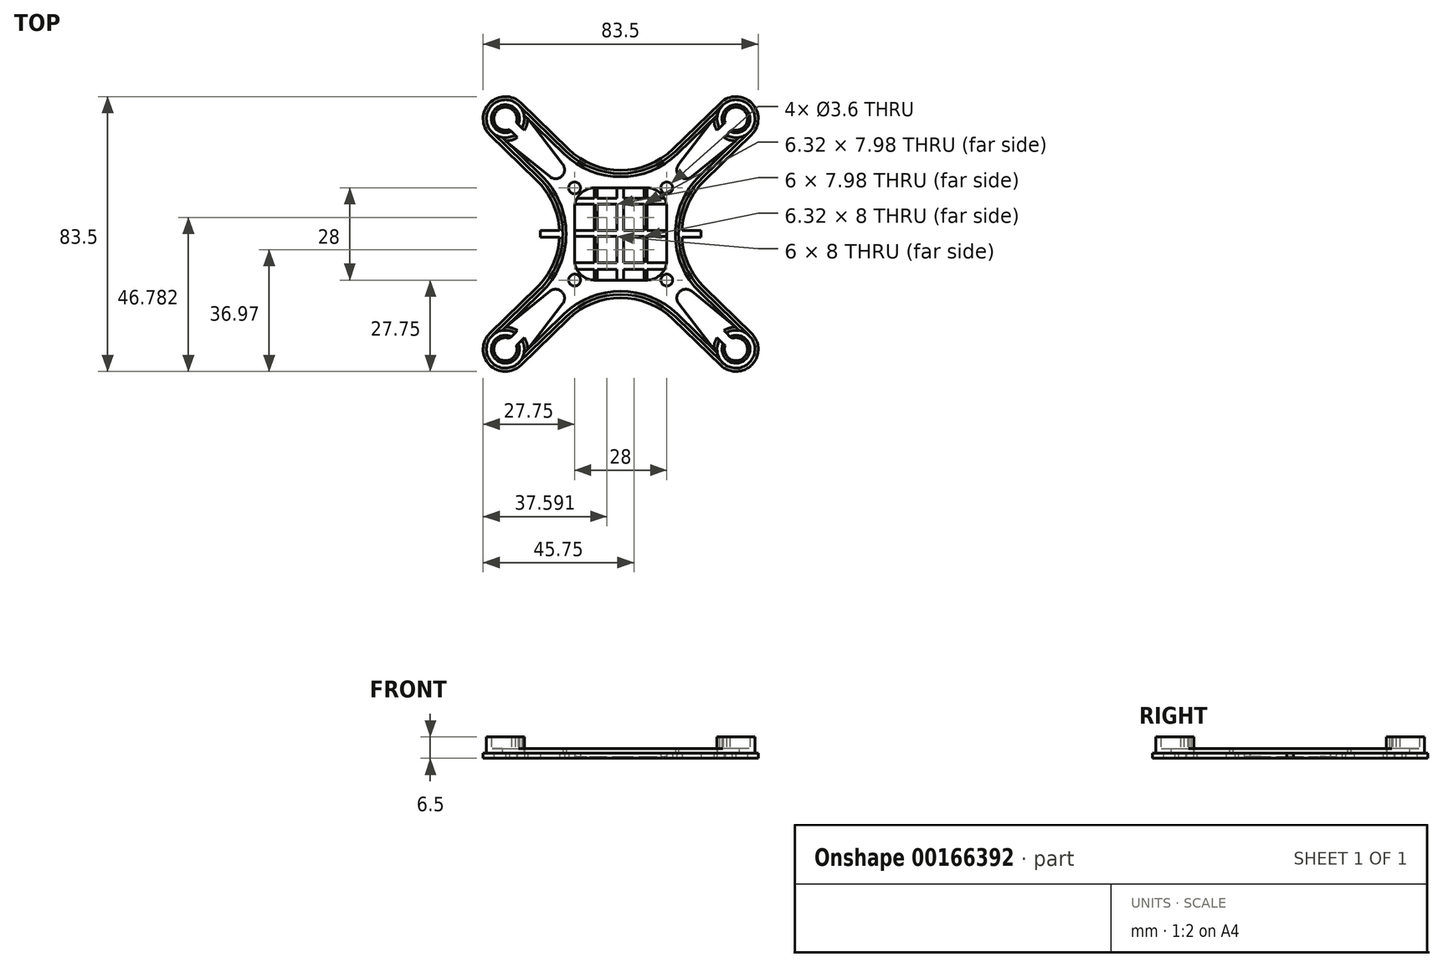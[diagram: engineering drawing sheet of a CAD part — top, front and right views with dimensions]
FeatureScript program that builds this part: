
annotation { "Feature Type Name" : "Feature", "Feature Type Description" : "" }
export const myFeature = defineFeature(function(context is Context, id is Id, definition is map)
    precondition{}
    {
        {
            var Q0;
            Q0=qCreatedBy(makeId("Top.planeOp"),FACE);
            var sketch = newSketch(context, id + "F0", { "sketchPlane" : qUnion([Q0])});
            skArc(sketch, "E0", {"start": v(31.69, -33.87) * mm, "mid": v(37.5, -37.44) * mm, "end": v(33.78, -31.72) * mm});
            skArc(sketch, "E1", {"start": v(29.24, -31.49) * mm, "mid": v(28.5, -33.2) * mm, "end": v(28.25, -35.06) * mm});
            skCircle(sketch, "E2", {"center": v(14, -14) * mm, "radius": 1.8 * mm});
            skLineSegment(sketch, "E3.0", {"start": v(39.7, -30.16) * mm, "end": v(25.47, -16.32) * mm});
            skLineSegment(sketch, "E4.0", {"start": v(30.3, -39.84) * mm, "end": v(15.88, -25.83) * mm});
            skArc(sketch, "E5", {"start": v(25.47, 16.32) * mm, "mid": v(18.58, 0) * mm, "end": v(25.47, -16.32) * mm});
            skArc(sketch, "E6.MirrorCS", {"start": v(-15.88, -25.83) * mm, "mid": v(0, -19.38) * mm, "end": v(15.88, -25.83) * mm});
            skPoint(sketch, "E7.orphan", {"position": v(7.32, -17.5) * mm});
            skArc(sketch, "E8", {"start": v(21.52, -17.39) * mm, "mid": v(17.87, -17.55) * mm, "end": v(17.6, -21.2) * mm});
            skLineSegment(sketch, "E9", {"start": v(31.69, -33.87) * mm, "end": v(29.24, -31.49) * mm});
            skLineSegment(sketch, "E10", {"start": v(31.33, -29.34) * mm, "end": v(33.78, -31.72) * mm});
            skArc(sketch, "E11.trimOffspring", {"start": v(34.87, -28.25) * mm, "mid": v(33.02, -28.55) * mm, "end": v(31.33, -29.34) * mm});
            skArc(sketch, "E12.trimOffspring", {"start": v(30.3, -39.84) * mm, "mid": v(39.84, -39.7) * mm, "end": v(39.7, -30.16) * mm});
            skLineSegment(sketch, "E13", {"start": v(8, -14) * mm, "end": v(-9, -14) * mm});
            skLineSegment(sketch, "E14", {"start": v(14, -8) * mm, "end": v(14, 9) * mm});
            skArc(sketch, "E15.filletArc", {"start": v(8, -14) * mm, "mid": v(12.24, -12.24) * mm, "end": v(14, -8) * mm});
            skLineSegment(sketch, "E16", {"start": v(28.25, -35.06) * mm, "end": v(17.6, -21.2) * mm});
            skLineSegment(sketch, "E17", {"start": v(34.87, -28.25) * mm, "end": v(21.52, -17.39) * mm});
            skLineSegment(sketch, "E18.MirrorCS", {"start": v(-31.33, -29.34) * mm, "end": v(-33.78, -31.72) * mm});
            skArc(sketch, "E19.MirrorCS", {"start": v(-29.24, -31.49) * mm, "mid": v(-28.5, -33.2) * mm, "end": v(-28.25, -35.06) * mm});
            skLineSegment(sketch, "E20.MirrorCS", {"start": v(-31.69, -33.87) * mm, "end": v(-29.24, -31.49) * mm});
            skArc(sketch, "E21.MirrorCS", {"start": v(-34.87, -28.25) * mm, "mid": v(-33.02, -28.55) * mm, "end": v(-31.33, -29.34) * mm});
            skLineSegment(sketch, "E22.MirrorCS", {"start": v(-34.87, -28.25) * mm, "end": v(-21.52, -17.39) * mm});
            skLineSegment(sketch, "E23.MirrorCS", {"start": v(-30.3, -39.84) * mm, "end": v(-15.88, -25.83) * mm});
            skArc(sketch, "E24.MirrorCS", {"start": v(-21.52, -17.39) * mm, "mid": v(-17.87, -17.55) * mm, "end": v(-17.6, -21.2) * mm});
            skLineSegment(sketch, "E25.MirrorCS", {"start": v(-39.7, -30.16) * mm, "end": v(-25.47, -16.32) * mm});
            skArc(sketch, "E26.MirrorCS", {"start": v(-31.69, -33.87) * mm, "mid": v(-37.5, -37.44) * mm, "end": v(-33.78, -31.72) * mm});
            skArc(sketch, "E27.MirrorCS", {"start": v(-30.3, -39.84) * mm, "mid": v(-39.84, -39.7) * mm, "end": v(-39.7, -30.16) * mm});
            skLineSegment(sketch, "E28.MirrorCS", {"start": v(-28.25, -35.06) * mm, "end": v(-17.6, -21.2) * mm});
            skCircle(sketch, "E29.MirrorC", {"center": v(-14, -14) * mm, "radius": 1.8 * mm});
            skArc(sketch, "E30.MirrorCS", {"start": v(-8, -14) * mm, "mid": v(-12.24, -12.24) * mm, "end": v(-14, -8) * mm});
            skArc(sketch, "E31.MirrorCS", {"start": v(-25.47, 16.32) * mm, "mid": v(-18.58, 0) * mm, "end": v(-25.47, -16.32) * mm});
            skLineSegment(sketch, "E32.MirrorCS", {"start": v(-14, -8) * mm, "end": v(-14, 9) * mm});
            skLineSegment(sketch, "E33.MirrorCS", {"start": v(-8, -14) * mm, "end": v(9, -14) * mm});
            skPoint(sketch, "E34.MirrorP", {"position": v(-7.32, -17.5) * mm});
            skLineSegment(sketch, "E35.MirrorCS", {"start": v(-31.69, 33.87) * mm, "end": v(-29.24, 31.49) * mm});
            skCircle(sketch, "E36.MirrorC", {"center": v(-14, 14) * mm, "radius": 1.8 * mm});
            skArc(sketch, "E37.MirrorCS", {"start": v(34.87, 28.25) * mm, "mid": v(33.02, 28.55) * mm, "end": v(31.33, 29.34) * mm});
            skLineSegment(sketch, "E38.MirrorCS", {"start": v(-31.33, 29.34) * mm, "end": v(-33.78, 31.72) * mm});
            skCircle(sketch, "E39.MirrorC", {"center": v(14, 14) * mm, "radius": 1.8 * mm});
            skLineSegment(sketch, "E40.MirrorCS", {"start": v(31.69, 33.87) * mm, "end": v(29.24, 31.49) * mm});
            skArc(sketch, "E41.MirrorCS", {"start": v(-34.87, 28.25) * mm, "mid": v(-33.02, 28.55) * mm, "end": v(-31.33, 29.34) * mm});
            skLineSegment(sketch, "E42.MirrorCS", {"start": v(31.33, 29.34) * mm, "end": v(33.78, 31.72) * mm});
            skArc(sketch, "E43.MirrorCS", {"start": v(29.24, 31.49) * mm, "mid": v(28.5, 33.2) * mm, "end": v(28.25, 35.06) * mm});
            skArc(sketch, "E44.MirrorCS", {"start": v(-29.24, 31.49) * mm, "mid": v(-28.5, 33.2) * mm, "end": v(-28.25, 35.06) * mm});
            skArc(sketch, "E45.MirrorCS", {"start": v(8, 14) * mm, "mid": v(12.24, 12.24) * mm, "end": v(14, 8) * mm});
            skArc(sketch, "E46.MirrorCS", {"start": v(-8, 14) * mm, "mid": v(-12.24, 12.24) * mm, "end": v(-14, 8) * mm});
            skLineSegment(sketch, "E47.MirrorCS", {"start": v(8, 14) * mm, "end": v(-9, 14) * mm});
            skPoint(sketch, "E48.MirrorP", {"position": v(7.32, 17.5) * mm});
            skArc(sketch, "E49.MirrorCS", {"start": v(21.52, 17.39) * mm, "mid": v(17.87, 17.55) * mm, "end": v(17.6, 21.2) * mm});
            skArc(sketch, "E50.MirrorCS", {"start": v(-30.3, 39.84) * mm, "mid": v(-39.84, 39.7) * mm, "end": v(-39.7, 30.16) * mm});
            skLineSegment(sketch, "E51.MirrorCS", {"start": v(34.87, 28.25) * mm, "end": v(21.52, 17.39) * mm});
            skPoint(sketch, "E52.MirrorP", {"position": v(-7.32, 17.5) * mm});
            skArc(sketch, "E53.MirrorCS", {"start": v(-15.88, 25.83) * mm, "mid": v(0, 19.38) * mm, "end": v(15.88, 25.83) * mm});
            skArc(sketch, "E54.MirrorCS", {"start": v(-21.52, 17.39) * mm, "mid": v(-17.87, 17.55) * mm, "end": v(-17.6, 21.2) * mm});
            skLineSegment(sketch, "E55.MirrorCS", {"start": v(-34.87, 28.25) * mm, "end": v(-21.52, 17.39) * mm});
            skLineSegment(sketch, "E56.MirrorCS", {"start": v(30.3, 39.84) * mm, "end": v(15.88, 25.83) * mm});
            skArc(sketch, "E57.MirrorCS", {"start": v(-31.69, 33.87) * mm, "mid": v(-37.5, 37.44) * mm, "end": v(-33.78, 31.72) * mm});
            skLineSegment(sketch, "E58.MirrorCS", {"start": v(-28.25, 35.06) * mm, "end": v(-17.6, 21.2) * mm});
            skLineSegment(sketch, "E59.MirrorCS", {"start": v(39.7, 30.16) * mm, "end": v(25.47, 16.32) * mm});
            skLineSegment(sketch, "E60.MirrorCS", {"start": v(-8, 14) * mm, "end": v(9, 14) * mm});
            skArc(sketch, "E61.MirrorCS", {"start": v(31.69, 33.87) * mm, "mid": v(37.5, 37.44) * mm, "end": v(33.78, 31.72) * mm});
            skLineSegment(sketch, "E62.MirrorCS", {"start": v(-39.7, 30.16) * mm, "end": v(-25.47, 16.32) * mm});
            skLineSegment(sketch, "E63.MirrorCS", {"start": v(-30.3, 39.84) * mm, "end": v(-15.88, 25.83) * mm});
            skLineSegment(sketch, "E64.MirrorCS", {"start": v(-14, 8) * mm, "end": v(-14, -9) * mm});
            skArc(sketch, "E65.MirrorCS", {"start": v(30.3, 39.84) * mm, "mid": v(39.84, 39.7) * mm, "end": v(39.7, 30.16) * mm});
            skLineSegment(sketch, "E66.MirrorCS", {"start": v(14, 8) * mm, "end": v(14, -9) * mm});
            skLineSegment(sketch, "E67.MirrorCS", {"start": v(28.25, 35.06) * mm, "end": v(17.6, 21.2) * mm});
            skLineSegment(sketch, "E68.bottom", {"start": v(18.4, 1) * mm, "end": v(24.4, 1) * mm});
            skLineSegment(sketch, "E68.top", {"start": v(18.4, -1) * mm, "end": v(24.4, -1) * mm});
            skLineSegment(sketch, "E68.left", {"start": v(18.4, 1) * mm, "end": v(18.4, -1) * mm});
            skLineSegment(sketch, "E68.right", {"start": v(24.4, 1) * mm, "end": v(24.4, -1) * mm});
            skLineSegment(sketch, "E69.MirrorCS", {"start": v(-18.4, 1) * mm, "end": v(-18.4, -1) * mm});
            skLineSegment(sketch, "E70.MirrorCS", {"start": v(-18.4, -1) * mm, "end": v(-24.4, -1) * mm});
            skLineSegment(sketch, "E71.MirrorCS", {"start": v(-24.4, 1) * mm, "end": v(-24.4, -1) * mm});
            skLineSegment(sketch, "E72.MirrorCS", {"start": v(-18.4, 1) * mm, "end": v(-24.4, 1) * mm});
            skSolve(sketch);
        }
        {
            var Q0;
            Q0 = qSketchRegion(id + "F0", true);
            extrude(context, id + "F1", {"entities" : qUnion([Q0]), "depth" : 1.5 * mm});
        }
        {
            var Q0;
            Q0=makeQuery(id+"F1.opExtrude","CAP_FACE",FACE,{"disambiguationData":[OSD([sQuery(id+"F0.wireOp",EDGE,"E0"),sQuery(id+"F0.wireOp",EDGE,"E1"),sQuery(id+"F0.wireOp",EDGE,"a01uJ8fQ-2ShT-JJJs-khPB-feFI2KhJfNbK"),sQuery(id+"F0.wireOp",EDGE,"Ob7BAK0L-Im8b-nV2W-ZPOP-jmZc5u1GQHVQ"),sQuery(id+"F0.wireOp",EDGE,"Yhxhbh3N-Pwvf-CZAK-NTRz-WfjfcWOoB3H8"),sQuery(id+"F0.wireOp",EDGE,"E2"),sQuery(id+"F0.wireOp",EDGE,"E3.0"),sQuery(id+"F0.wireOp",EDGE,"E4.0"),sQuery(id+"F0.wireOp",EDGE,"921c4a34-4074-4e6a-8ea0-2c27b11e1a93.0"),sQuery(id+"F0.wireOp",EDGE,"8042876e-c550-468f-ba5b-50dd2e758e40.0"),sQuery(id+"F0.wireOp",EDGE,"E5"),sQuery(id+"F0.wireOp",EDGE,"b88f5849-8e9e-4a16-b14d-f28babdcc0c70.MirrorCS"),sQuery(id+"F0.wireOp",EDGE,"b88f5849-8e9e-4a16-b14d-f28babdcc0c71.MirrorCS"),sQuery(id+"F0.wireOp",EDGE,"b88f5849-8e9e-4a16-b14d-f28babdcc0c74.MirrorCS"),sQuery(id+"F0.wireOp",EDGE,"b88f5849-8e9e-4a16-b14d-f28babdcc0c75.MirrorCS"),sQuery(id+"F0.wireOp",EDGE,"b8554301-71cc-457b-a27f-fdabd42372d80.MirrorCS"),sQuery(id+"F0.wireOp",EDGE,"8d917b84-10ed-46aa-9923-405c7a226399.filletArc"),sQuery(id+"F0.wireOp",EDGE,"E6.MirrorCS"),sQuery(id+"F0.wireOp",EDGE,"a4643b09-8a2d-470e-a5d3-b5b7147de01a.trimOffspring"),sQuery(id+"F0.wireOp",EDGE,"e1d1502e-aa15-4543-9f89-ce20ea1ce206.trimOffspring"),sQuery(id+"F0.wireOp",EDGE,"E8"),sQuery(id+"F0.wireOp",EDGE,"432c7407-925d-4150-9526-7c587b8a6b590.MirrorCS"),sQuery(id+"F0.wireOp",EDGE,"432c7407-925d-4150-9526-7c587b8a6b591.MirrorCS"),sQuery(id+"F0.wireOp",EDGE,"432c7407-925d-4150-9526-7c587b8a6b592.MirrorCS"),sQuery(id+"F0.wireOp",EDGE,"84ef0a4b-eb97-41a7-a49f-92f9b87771770.MirrorCS"),sQuery(id+"F0.wireOp",EDGE,"84ef0a4b-eb97-41a7-a49f-92f9b87771771.MirrorCS"),sQuery(id+"F0.wireOp",EDGE,"84ef0a4b-eb97-41a7-a49f-92f9b87771772.MirrorCS"),sQuery(id+"F0.wireOp",EDGE,"84ef0a4b-eb97-41a7-a49f-92f9b87771773.MirrorCS"),sQuery(id+"F0.wireOp",EDGE,"84ef0a4b-eb97-41a7-a49f-92f9b87771774.MirrorCS"),sQuery(id+"F0.wireOp",EDGE,"84ef0a4b-eb97-41a7-a49f-92f9b87771775.MirrorCS"),sQuery(id+"F0.wireOp",EDGE,"feb3afbb-cc8c-4bbc-aa67-0586ad6dce8c.0"),sQuery(id+"F0.wireOp",EDGE,"a1452b85-d45b-435e-881a-8c6a6ef33bc9.0"),sQuery(id+"F0.wireOp",EDGE,"64c3a18d-b4ba-416d-8e09-7861b4cc0028.0"),sQuery(id+"F0.wireOp",EDGE,"76b5986a-2c51-4484-8229-e95649198d5d.0"),sQuery(id+"F0.wireOp",EDGE,"E9"),sQuery(id+"F0.wireOp",EDGE,"E10"),sQuery(id+"F0.wireOp",EDGE,"E11.trimOffspring"),sQuery(id+"F0.wireOp",EDGE,"E12.trimOffspring"),sQuery(id+"F0.wireOp",EDGE,"e6a221e6-ec1e-47e5-89df-8c310038d3240.MirrorCS"),sQuery(id+"F0.wireOp",EDGE,"e6a221e6-ec1e-47e5-89df-8c310038d3241.MirrorCS"),sQuery(id+"F0.wireOp",EDGE,"e6a221e6-ec1e-47e5-89df-8c310038d3242.MirrorCS"),sQuery(id+"F0.wireOp",EDGE,"e6a221e6-ec1e-47e5-89df-8c310038d3244.MirrorCS"),sQuery(id+"F0.wireOp",EDGE,"e6a221e6-ec1e-47e5-89df-8c310038d3245.MirrorCS"),sQuery(id+"F0.wireOp",EDGE,"e6a221e6-ec1e-47e5-89df-8c310038d3246.MirrorCS"),sQuery(id+"F0.wireOp",EDGE,"1c5d13f6-029d-4adf-95b2-7eb6a2bd37fe0.MirrorCS"),sQuery(id+"F0.wireOp",EDGE,"1c5d13f6-029d-4adf-95b2-7eb6a2bd37fe1.MirrorCS"),sQuery(id+"F0.wireOp",EDGE,"1c5d13f6-029d-4adf-95b2-7eb6a2bd37fe2.MirrorCS"),sQuery(id+"F0.wireOp",EDGE,"1c5d13f6-029d-4adf-95b2-7eb6a2bd37fe3.MirrorCS"),sQuery(id+"F0.wireOp",EDGE,"1c5d13f6-029d-4adf-95b2-7eb6a2bd37fe5.MirrorCS"),sQuery(id+"F0.wireOp",EDGE,"1c5d13f6-029d-4adf-95b2-7eb6a2bd37fe6.MirrorCS"),sQuery(id+"F0.wireOp",EDGE,"1c5d13f6-029d-4adf-95b2-7eb6a2bd37fe7.MirrorCS"),sQuery(id+"F0.wireOp",EDGE,"1c5d13f6-029d-4adf-95b2-7eb6a2bd37fe8.MirrorCS"),sQuery(id+"F0.wireOp",EDGE,"1c5d13f6-029d-4adf-95b2-7eb6a2bd37fe9.MirrorCS"),sQuery(id+"F0.wireOp",EDGE,"1c5d13f6-029d-4adf-95b2-7eb6a2bd37fe10.MirrorCS"),sQuery(id+"F0.wireOp",EDGE,"1c5d13f6-029d-4adf-95b2-7eb6a2bd37fe12.MirrorCS"),sQuery(id+"F0.wireOp",EDGE,"1c5d13f6-029d-4adf-95b2-7eb6a2bd37fe13.MirrorCS")])],"isStart":false});
            var sketch = newSketch(context, id + "F2", { "sketchPlane" : qUnion([Q0])});
            skLineSegment(sketch, "E73.0", {"start": v(32.07, -30.06) * mm, "end": v(33.2, -31.15) * mm});
            skLineSegment(sketch, "E73.1", {"start": v(31.1, -33.3) * mm, "end": v(29.97, -32.2) * mm});
            skArc(sketch, "E74", {"start": v(31.1, -33.3) * mm, "mid": v(38.05, -37.96) * mm, "end": v(33.2, -31.15) * mm});
            skArc(sketch, "E75", {"start": v(29.97, -32.2) * mm, "mid": v(39.12, -39) * mm, "end": v(32.07, -30.06) * mm});
            skLineSegment(sketch, "E76.MirrorCS", {"start": v(-32.07, -30.06) * mm, "end": v(-33.2, -31.15) * mm});
            skLineSegment(sketch, "E77.MirrorCS", {"start": v(-31.1, -33.3) * mm, "end": v(-29.97, -32.2) * mm});
            skArc(sketch, "E78.MirrorCS", {"start": v(-31.1, -33.3) * mm, "mid": v(-38.05, -37.96) * mm, "end": v(-33.2, -31.15) * mm});
            skArc(sketch, "E79.MirrorCS", {"start": v(-29.97, -32.2) * mm, "mid": v(-39.12, -39) * mm, "end": v(-32.07, -30.06) * mm});
            skLineSegment(sketch, "E80.MirrorCS", {"start": v(32.07, 30.06) * mm, "end": v(33.2, 31.15) * mm});
            skLineSegment(sketch, "E81.MirrorCS", {"start": v(31.1, 33.3) * mm, "end": v(29.97, 32.2) * mm});
            skLineSegment(sketch, "E82.MirrorCS", {"start": v(-31.1, 33.3) * mm, "end": v(-29.97, 32.2) * mm});
            skLineSegment(sketch, "E83.MirrorCS", {"start": v(-32.07, 30.06) * mm, "end": v(-33.2, 31.15) * mm});
            skArc(sketch, "E84.MirrorCS", {"start": v(31.1, 33.3) * mm, "mid": v(38.05, 37.96) * mm, "end": v(33.2, 31.15) * mm});
            skArc(sketch, "E85.MirrorCS", {"start": v(-29.97, 32.2) * mm, "mid": v(-39.12, 39) * mm, "end": v(-32.07, 30.06) * mm});
            skArc(sketch, "E86.MirrorCS", {"start": v(29.97, 32.2) * mm, "mid": v(39.12, 39) * mm, "end": v(32.07, 30.06) * mm});
            skArc(sketch, "E87.MirrorCS", {"start": v(-31.1, 33.3) * mm, "mid": v(-38.05, 37.96) * mm, "end": v(-33.2, 31.15) * mm});
            skSolve(sketch);
        }
        {
            var Q0;
            Q0 = qSketchRegion(id + "F2", true);
            extrude(context, id + "F3", {"entities" : qUnion([Q0]), "operationType" : NewBodyOperationType.ADD, "depth" : 5 * mm});
        }
        {
            var Q0;
            Q0=qCreatedBy(makeId("Top.planeOp"),FACE);
            var sketch = newSketch(context, id + "F4", { "sketchPlane" : qUnion([Q0])});
            skLineSegment(sketch, "E88.0", {"start": v(0.84, -8.78) * mm, "end": v(0.84, -0.78) * mm});
            skLineSegment(sketch, "E89.0", {"start": v(-1.16, -8.78) * mm, "end": v(-1.16, -0.78) * mm});
            skLineSegment(sketch, "E90.1.0.0", {"start": v(7.16, -8.78) * mm, "end": v(7.16, -0.78) * mm});
            skLineSegment(sketch, "E90.1.0.1", {"start": v(8, -14) * mm, "end": v(8, -10.78) * mm});
            skLineSegment(sketch, "E91.MirrorCS", {"start": v(-7.16, -8.78) * mm, "end": v(-7.16, -0.78) * mm});
            skLineSegment(sketch, "E92.MirrorCS", {"start": v(-8, -8.78) * mm, "end": v(-8, -0.78) * mm});
            skLineSegment(sketch, "E93.0", {"start": v(-14, 1.04) * mm, "end": v(-8, 1.04) * mm});
            skLineSegment(sketch, "E94.0", {"start": v(-14, -0.78) * mm, "end": v(-8, -0.78) * mm});
            skLineSegment(sketch, "E95.0", {"start": v(-13.91, 9.02) * mm, "end": v(-8, 9.02) * mm});
            skLineSegment(sketch, "E96.0", {"start": v(-13.27, 10.88) * mm, "end": v(-8, 10.88) * mm});
            skLineSegment(sketch, "E97.0", {"start": v(-14, -8.78) * mm, "end": v(-8, -8.78) * mm});
            skLineSegment(sketch, "E98.0", {"start": v(-13.32, -10.78) * mm, "end": v(-8, -10.78) * mm});
            skPoint(sketch, "E99.5", {"position": v(8, -14) * mm});
            skPoint(sketch, "E100.orphan", {"position": v(-8, 14.56) * mm});
            skPoint(sketch, "E101.orphan", {"position": v(-7.16, 14.78) * mm});
            skPoint(sketch, "E102.orphan", {"position": v(0.84, 14.62) * mm});
            skPoint(sketch, "E103.orphan", {"position": v(-1.16, 14.78) * mm});
            skPoint(sketch, "E104.orphan", {"position": v(7.16, 14.78) * mm});
            skPoint(sketch, "E105.orphan", {"position": v(8, 14.56) * mm});
            skPoint(sketch, "E106.orphan", {"position": v(8, -14.52) * mm});
            skPoint(sketch, "E107.orphan", {"position": v(0.84, -14.46) * mm});
            skPoint(sketch, "E108.orphan", {"position": v(-7.16, -14.3) * mm});
            skPoint(sketch, "E109.orphan", {"position": v(-8, -14.52) * mm});
            skLineSegment(sketch, "E110.trimOffspring", {"start": v(-7.16, 10.88) * mm, "end": v(-1.16, 10.88) * mm});
            skLineSegment(sketch, "E111.trimOffspring", {"start": v(-7.16, 10.88) * mm, "end": v(-7.16, 14) * mm});
            skLineSegment(sketch, "E112.trimOffspring", {"start": v(-7.16, 9.02) * mm, "end": v(-1.16, 9.02) * mm});
            skLineSegment(sketch, "E113.trimOffspring", {"start": v(-8, 10.88) * mm, "end": v(-8, 14) * mm});
            skLineSegment(sketch, "E114.trimOffspring", {"start": v(-1.16, 10.88) * mm, "end": v(-1.16, 14) * mm});
            skLineSegment(sketch, "E115.trimOffspring", {"start": v(0.84, 10.88) * mm, "end": v(0.84, 14) * mm});
            skLineSegment(sketch, "E116.trimOffspring", {"start": v(0.84, 9.02) * mm, "end": v(7.16, 9.02) * mm});
            skLineSegment(sketch, "E117.trimOffspring", {"start": v(0.84, 10.88) * mm, "end": v(7.16, 10.88) * mm});
            skLineSegment(sketch, "E118.trimOffspring", {"start": v(8, 10.88) * mm, "end": v(13.94, 10.88) * mm});
            skLineSegment(sketch, "E119.trimOffspring", {"start": v(8, 9.02) * mm, "end": v(13.91, 9.02) * mm});
            skLineSegment(sketch, "E120.trimOffspring", {"start": v(8, 10.88) * mm, "end": v(8, 14) * mm});
            skLineSegment(sketch, "E121.trimOffspring", {"start": v(7.16, 10.88) * mm, "end": v(7.16, 14) * mm});
            skLineSegment(sketch, "E122.trimOffspring", {"start": v(8, -0.78) * mm, "end": v(14, -0.78) * mm});
            skLineSegment(sketch, "E123.trimOffspring", {"start": v(0.84, 1.04) * mm, "end": v(7.16, 1.04) * mm});
            skLineSegment(sketch, "E124.trimOffspring", {"start": v(0.84, -0.78) * mm, "end": v(7.16, -0.78) * mm});
            skLineSegment(sketch, "E125.trimOffspring", {"start": v(8, 1.04) * mm, "end": v(14, 1.04) * mm});
            skLineSegment(sketch, "E126.trimOffspring", {"start": v(-7.16, 1.04) * mm, "end": v(-1.16, 1.04) * mm});
            skLineSegment(sketch, "E127.trimOffspring", {"start": v(-7.16, -0.78) * mm, "end": v(-1.16, -0.78) * mm});
            skLineSegment(sketch, "E128.trimOffspring", {"start": v(-7.16, -8.78) * mm, "end": v(-1.16, -8.78) * mm});
            skLineSegment(sketch, "E129.trimOffspring", {"start": v(8, -8.78) * mm, "end": v(8, -0.78) * mm});
            skLineSegment(sketch, "E130.trimOffspring", {"start": v(0.84, -8.78) * mm, "end": v(7.16, -8.78) * mm});
            skLineSegment(sketch, "E131", {"start": v(-7.16, -10.78) * mm, "end": v(-7.16, -14) * mm});
            skLineSegment(sketch, "E132.trimOffspring", {"start": v(-7.16, -10.78) * mm, "end": v(-1.16, -10.78) * mm});
            skLineSegment(sketch, "E133.trimOffspring", {"start": v(-8, -10.78) * mm, "end": v(-8, -14) * mm});
            skLineSegment(sketch, "E134", {"start": v(-1.16, -10.78) * mm, "end": v(-1.16, -14) * mm});
            skLineSegment(sketch, "E135", {"start": v(0.84, -10.78) * mm, "end": v(0.84, -14) * mm});
            skLineSegment(sketch, "E136", {"start": v(7.16, -10.78) * mm, "end": v(7.16, -14) * mm});
            skLineSegment(sketch, "E137.trimOffspring", {"start": v(0.84, -10.78) * mm, "end": v(7.16, -10.78) * mm});
            skLineSegment(sketch, "E138.trimOffspring", {"start": v(8, -10.78) * mm, "end": v(13.9, -10.78) * mm});
            skLineSegment(sketch, "E139.trimOffspring", {"start": v(7.16, 1.04) * mm, "end": v(7.16, 9.02) * mm});
            skLineSegment(sketch, "E140.trimOffspring", {"start": v(8, 1.04) * mm, "end": v(8, 9.02) * mm});
            skLineSegment(sketch, "E141.trimOffspring", {"start": v(-7.16, 1.04) * mm, "end": v(-7.16, 9.02) * mm});
            skLineSegment(sketch, "E142.trimOffspring", {"start": v(-8, 1.04) * mm, "end": v(-8, 9.02) * mm});
            skLineSegment(sketch, "E143.trimOffspring", {"start": v(-1.16, 1.04) * mm, "end": v(-1.16, 9.02) * mm});
            skLineSegment(sketch, "E144.trimOffspring", {"start": v(0.84, 1.04) * mm, "end": v(0.84, 9.02) * mm});
            skPoint(sketch, "E145.orphan", {"position": v(7.16, -14.3) * mm});
            skLineSegment(sketch, "E146.0", {"start": v(-8, -14) * mm, "end": v(8, -14) * mm});
            skArc(sketch, "E146.1", {"start": v(8, -14) * mm, "mid": v(12.24, -12.24) * mm, "end": v(14, -8) * mm});
            skLineSegment(sketch, "E146.2", {"start": v(14, 8) * mm, "end": v(14, -8) * mm});
            skArc(sketch, "E146.3", {"start": v(8, 14) * mm, "mid": v(12.24, 12.24) * mm, "end": v(14, 8) * mm});
            skLineSegment(sketch, "E146.4", {"start": v(-8, 14) * mm, "end": v(8, 14) * mm});
            skArc(sketch, "E146.5", {"start": v(-8, 14) * mm, "mid": v(-12.24, 12.24) * mm, "end": v(-14, 8) * mm});
            skLineSegment(sketch, "E146.6", {"start": v(-14, 8) * mm, "end": v(-14, -8) * mm});
            skArc(sketch, "E146.7", {"start": v(-8, -14) * mm, "mid": v(-12.24, -12.24) * mm, "end": v(-14, -8) * mm});
            skPoint(sketch, "E146.8", {"position": v(-12.24, -12.24) * mm});
            skLineSegment(sketch, "E147", {"start": v(8, -8.78) * mm, "end": v(14, -8.78) * mm});
            skLineSegment(sketch, "E148.trimOffspring", {"start": v(-8, 14.56) * mm, "end": v(-8, 14.63) * mm});
            skSolve(sketch);
        }
        {
            var Q0;
            Q0=makeQuery(id+"F4.imprint","IMPRINT",FACE,{"disambiguationData":[TD([[makeQuery(id+"F4.imprint","IMPRINT",EDGE,{"derivedFrom":sQuery(id+"F4.wireOp",EDGE,"E88.0")}),1.0]])]});
            extrude(context, id + "F5", {"entities" : qUnion([Q0]), "operationType" : NewBodyOperationType.ADD, "depth" : .5 * mm});
        }
        {
            var Q0;
            {var subQ0=sQuery(id+"F0.wireOp",EDGE,"E55.MirrorCS");var subQ1=sQuery(id+"F0.wireOp",EDGE,"E50.MirrorCS");var subQ2=sQuery(id+"F0.wireOp",EDGE,"E46.MirrorCS");var subQ3=sQuery(id+"F0.wireOp",EDGE,"E54.MirrorCS");var subQ4=sQuery(id+"F0.wireOp",EDGE,"E44.MirrorCS");var subQ5=sQuery(id+"F0.wireOp",EDGE,"E45.MirrorCS");var subQ6=sQuery(id+"F0.wireOp",EDGE,"E43.MirrorCS");var subQ7=sQuery(id+"F0.wireOp",EDGE,"E51.MirrorCS");var subQ8=sQuery(id+"F0.wireOp",EDGE,"E41.MirrorCS");var subQ9=sQuery(id+"F0.wireOp",EDGE,"E39.MirrorC");var subQ10=sQuery(id+"F0.wireOp",EDGE,"E37.MirrorCS");var subQ11=sQuery(id+"F0.wireOp",EDGE,"E35.MirrorCS");var subQ12=sQuery(id+"F0.wireOp",EDGE,"E28.MirrorCS");var subQ13=sQuery(id+"F0.wireOp",EDGE,"E31.MirrorCS");var subQ14=sQuery(id+"F0.wireOp",EDGE,"E53.MirrorCS");var subQ15=sQuery(id+"F0.wireOp",EDGE,"E42.MirrorCS");var subQ16=sQuery(id+"F0.wireOp",EDGE,"E40.MirrorCS");var subQ17=sQuery(id+"F0.wireOp",EDGE,"E30.MirrorCS");var subQ18=sQuery(id+"F0.wireOp",EDGE,"E29.MirrorC");var subQ19=sQuery(id+"F0.wireOp",EDGE,"E38.MirrorCS");var subQ20=sQuery(id+"F0.wireOp",EDGE,"E36.MirrorC");var subQ21=sQuery(id+"F0.wireOp",EDGE,"E27.MirrorCS");var subQ22=sQuery(id+"F0.wireOp",EDGE,"E10");var subQ23=sQuery(id+"F0.wireOp",EDGE,"E8");var subQ24=sQuery(id+"F0.wireOp",EDGE,"E67.MirrorCS");var subQ25=sQuery(id+"F0.wireOp",EDGE,"E17");var subQ26=sQuery(id+"F0.wireOp",EDGE,"E6.MirrorCS");var subQ27=sQuery(id+"F0.wireOp",EDGE,"E5");var subQ28=sQuery(id+"F0.wireOp",EDGE,"E19.MirrorCS");var subQ29=sQuery(id+"F0.wireOp",EDGE,"E9");var subQ30=sQuery(id+"F0.wireOp",EDGE,"E1");var subQ31=sQuery(id+"F0.wireOp",EDGE,"E2");var subQ32=sQuery(id+"F0.wireOp",EDGE,"E49.MirrorCS");var subQ33=sQuery(id+"F0.wireOp",EDGE,"E3.0");var subQ34=sQuery(id+"F0.wireOp",EDGE,"E4.0");var subQ35=sQuery(id+"F0.wireOp",EDGE,"E25.MirrorCS");var subQ36=sQuery(id+"F0.wireOp",EDGE,"E12.trimOffspring");var subQ37=sQuery(id+"F0.wireOp",EDGE,"E18.MirrorCS");var subQ38=sQuery(id+"F0.wireOp",EDGE,"E66.MirrorCS");var subQ39=sQuery(id+"F0.wireOp",EDGE,"E20.MirrorCS");var subQ40=sQuery(id+"F0.wireOp",EDGE,"E11.trimOffspring");var subQ41=sQuery(id+"F0.wireOp",EDGE,"E21.MirrorCS");var subQ42=sQuery(id+"F0.wireOp",EDGE,"E33.MirrorCS");var subQ43=sQuery(id+"F0.wireOp",EDGE,"E24.MirrorCS");var subQ44=sQuery(id+"F0.wireOp",EDGE,"E22.MirrorCS");var subQ45=sQuery(id+"F0.wireOp",EDGE,"E16");var subQ46=sQuery(id+"F0.wireOp",EDGE,"E15.filletArc");var subQ47=sQuery(id+"F0.wireOp",EDGE,"E23.MirrorCS");var subQ48=sQuery(id+"F0.wireOp",EDGE,"E56.MirrorCS");var subQ49=sQuery(id+"F0.wireOp",EDGE,"E58.MirrorCS");var subQ50=sQuery(id+"F0.wireOp",EDGE,"E59.MirrorCS");var subQ51=sQuery(id+"F0.wireOp",EDGE,"E60.MirrorCS");var subQ52=sQuery(id+"F0.wireOp",EDGE,"E62.MirrorCS");var subQ53=sQuery(id+"F0.wireOp",EDGE,"E63.MirrorCS");var subQ54=sQuery(id+"F0.wireOp",EDGE,"E64.MirrorCS");var subQ55=sQuery(id+"F0.wireOp",EDGE,"E65.MirrorCS");Q0=makeQuery(id+"F3.boolean.opBoolean","SPLIT",FACE,{"disambiguationData":[TD([makeQuery(id+"F1.opExtrude","SWEPT_FACE",FACE,{"disambiguationData":[OSD([subQ30])]})])],"derivedFrom":makeQuery(id+"F1.opExtrude","CAP_FACE",FACE,{"disambiguationData":[OSD([sQuery(id+"F0.wireOp",EDGE,"E0"),subQ30,subQ31,subQ33,subQ34,subQ27,subQ26,subQ23,subQ29,subQ22,subQ40,subQ36,subQ46,subQ45,subQ25,subQ37,subQ28,subQ39,subQ41,subQ44,subQ47,subQ43,subQ35,sQuery(id+"F0.wireOp",EDGE,"E26.MirrorCS"),subQ21,subQ12,subQ18,subQ17,subQ13,subQ42,subQ11,subQ20,subQ10,subQ19,subQ9,subQ16,subQ8,subQ15,subQ6,subQ4,subQ5,subQ2,subQ32,subQ1,subQ7,subQ14,subQ3,subQ0,subQ48,sQuery(id+"F0.wireOp",EDGE,"E57.MirrorCS"),subQ49,subQ50,subQ51,sQuery(id+"F0.wireOp",EDGE,"E61.MirrorCS"),subQ52,subQ53,subQ54,subQ55,subQ38,subQ24])],"isStart":false})});}
            var sketch = newSketch(context, id + "F6", { "sketchPlane" : qUnion([Q0])});
            skLineSegment(sketch, "E149.0", {"start": v(-31, 39.12) * mm, "end": v(-16.58, 25.11) * mm});
            skLineSegment(sketch, "E150.0", {"start": v(31, 39.12) * mm, "end": v(16.58, 25.11) * mm});
            skArc(sketch, "E150.1", {"start": v(-16.58, 25.11) * mm, "mid": v(0, 18.38) * mm, "end": v(16.58, 25.11) * mm});
            skLineSegment(sketch, "E151.0", {"start": v(39, -30.88) * mm, "end": v(24.78, -17.04) * mm});
            skArc(sketch, "E151.1", {"start": v(24.78, 17.04) * mm, "mid": v(17.58, 0) * mm, "end": v(24.78, -17.04) * mm});
            skLineSegment(sketch, "E151.2", {"start": v(39, 30.88) * mm, "end": v(24.78, 17.04) * mm});
            skLineSegment(sketch, "E152.0", {"start": v(-31, -39.12) * mm, "end": v(-16.58, -25.11) * mm});
            skArc(sketch, "E152.1", {"start": v(-16.58, -25.11) * mm, "mid": v(0, -18.38) * mm, "end": v(16.58, -25.11) * mm});
            skLineSegment(sketch, "E152.2", {"start": v(31, -39.12) * mm, "end": v(16.58, -25.11) * mm});
            skLineSegment(sketch, "E153.0", {"start": v(-39, 30.88) * mm, "end": v(-24.78, 17.04) * mm});
            skArc(sketch, "E153.1", {"start": v(-24.78, 17.04) * mm, "mid": v(-17.58, 0) * mm, "end": v(-24.78, -17.04) * mm});
            skLineSegment(sketch, "E153.2", {"start": v(-39, -30.88) * mm, "end": v(-24.78, -17.04) * mm});
            skLineSegment(sketch, "E154.0", {"start": v(29.37, 36.15) * mm, "end": v(17.28, 24.4) * mm});
            skArc(sketch, "E154.1", {"start": v(-17.28, 24.4) * mm, "mid": v(0, 17.38) * mm, "end": v(17.28, 24.4) * mm});
            skLineSegment(sketch, "E154.2", {"start": v(-29.37, 36.15) * mm, "end": v(-17.28, 24.4) * mm});
            skLineSegment(sketch, "E155.0", {"start": v(35.99, -29.34) * mm, "end": v(24.08, -17.76) * mm});
            skArc(sketch, "E155.1", {"start": v(24.08, 17.76) * mm, "mid": v(16.58, 0) * mm, "end": v(24.08, -17.76) * mm});
            skLineSegment(sketch, "E155.2", {"start": v(35.99, 29.34) * mm, "end": v(24.08, 17.76) * mm});
            skLineSegment(sketch, "E156.0", {"start": v(-29.37, -36.15) * mm, "end": v(-17.28, -24.4) * mm});
            skArc(sketch, "E156.1", {"start": v(-17.28, -24.4) * mm, "mid": v(0, -17.38) * mm, "end": v(17.28, -24.4) * mm});
            skLineSegment(sketch, "E156.2", {"start": v(29.37, -36.15) * mm, "end": v(17.28, -24.4) * mm});
            skLineSegment(sketch, "E157.0", {"start": v(-35.99, 29.34) * mm, "end": v(-24.08, 17.76) * mm});
            skArc(sketch, "E157.1", {"start": v(-24.08, 17.76) * mm, "mid": v(-16.58, 0) * mm, "end": v(-24.08, -17.76) * mm});
            skLineSegment(sketch, "E157.2", {"start": v(-35.99, -29.34) * mm, "end": v(-24.08, -17.76) * mm});
            skArc(sketch, "E158.0", {"start": v(-29.37, 36.15) * mm, "mid": v(-29.95, 37.76) * mm, "end": v(-31, 39.12) * mm});
            skArc(sketch, "E158.1", {"start": v(-29.37, -36.15) * mm, "mid": v(-29.95, -37.76) * mm, "end": v(-31, -39.12) * mm});
            skArc(sketch, "E158.2", {"start": v(29.37, -36.15) * mm, "mid": v(29.95, -37.76) * mm, "end": v(31, -39.12) * mm});
            skArc(sketch, "E158.3", {"start": v(29.37, 36.15) * mm, "mid": v(29.95, 37.76) * mm, "end": v(31, 39.12) * mm});
            skArc(sketch, "E159.trimOffspring", {"start": v(-39, 30.88) * mm, "mid": v(-37.61, 29.88) * mm, "end": v(-35.99, 29.34) * mm});
            skArc(sketch, "E160.trimOffspring", {"start": v(39, 30.88) * mm, "mid": v(37.61, 29.88) * mm, "end": v(35.99, 29.34) * mm});
            skArc(sketch, "E161.trimOffspring", {"start": v(39, -30.88) * mm, "mid": v(37.61, -29.88) * mm, "end": v(35.99, -29.34) * mm});
            skArc(sketch, "E162.trimOffspring", {"start": v(-39, -30.88) * mm, "mid": v(-37.61, -29.88) * mm, "end": v(-35.99, -29.34) * mm});
            skPoint(sketch, "E163.orphan", {"position": v(-29.97, 32.2) * mm});
            skPoint(sketch, "E164.orphan", {"position": v(-32.07, 30.06) * mm});
            skPoint(sketch, "E165.orphan", {"position": v(29.97, 32.2) * mm});
            skPoint(sketch, "E166.orphan", {"position": v(32.07, 30.06) * mm});
            skPoint(sketch, "E167.orphan", {"position": v(32.07, -30.06) * mm});
            skPoint(sketch, "E168.orphan", {"position": v(29.97, -32.2) * mm});
            skPoint(sketch, "E169.orphan", {"position": v(-29.97, -32.2) * mm});
            skPoint(sketch, "E170.orphan", {"position": v(-32.07, -30.06) * mm});
            skSolve(sketch);
        }
        {
            var Q0;
            Q0 = qSketchRegion(id + "F6", true);
            extrude(context, id + "F7", {"entities" : qUnion([Q0]), "operationType" : NewBodyOperationType.ADD, "depth" : 1.5 * mm});
        }
    });
